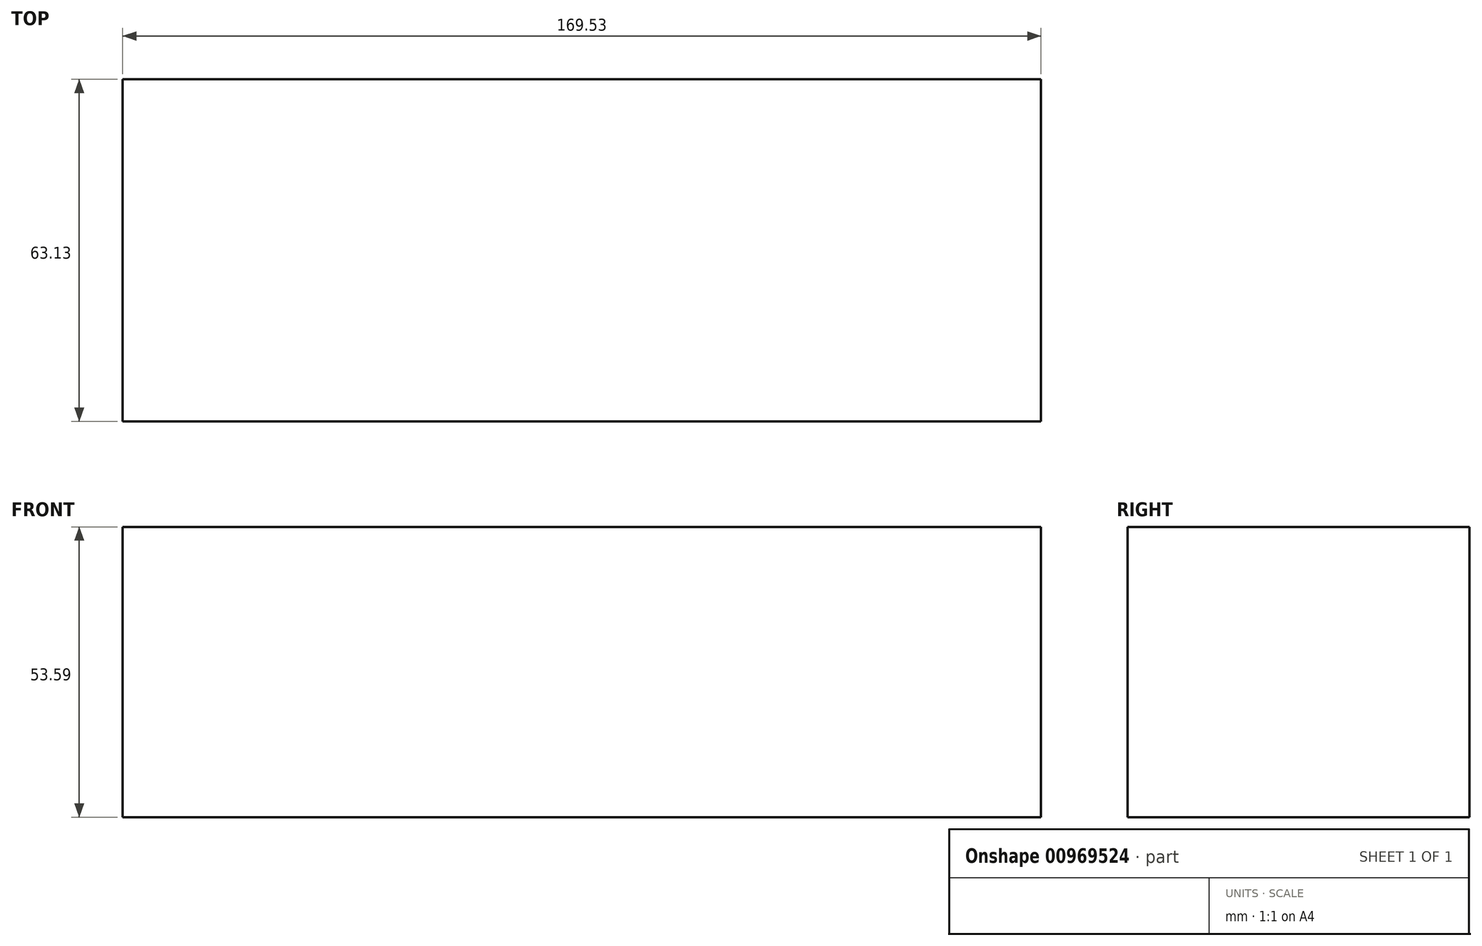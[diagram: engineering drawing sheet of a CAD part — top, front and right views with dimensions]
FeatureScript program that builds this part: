
annotation { "Feature Type Name" : "Feature", "Feature Type Description" : "" }
export const myFeature = defineFeature(function(context is Context, id is Id, definition is map)
    precondition{}
    {
        {
            var Q0;
            Q0=qCreatedBy(makeId("Top.planeOp"),FACE);
            var sketch = newSketch(context, id + "F0", { "sketchPlane" : qUnion([Q0])});
            skLineSegment(sketch, "E0.bottom", {"start": v(-103.93, -21.12) * mm, "end": v(65.6, -21.12) * mm});
            skLineSegment(sketch, "E0.top", {"start": v(-103.93, 42) * mm, "end": v(65.6, 42) * mm});
            skLineSegment(sketch, "E0.left", {"start": v(-103.93, -21.12) * mm, "end": v(-103.93, 42) * mm});
            skLineSegment(sketch, "E0.right", {"start": v(65.6, -21.12) * mm, "end": v(65.6, 42) * mm});
            skSolve(sketch);
        }
        {
            var Q0;
            Q0=makeQuery(id+"F0.imprint","IMPRINT",FACE,{"disambiguationData":[TD([[makeQuery(id+"F0.imprint","IMPRINT",EDGE,{"derivedFrom":sQuery(id+"F0.wireOp",EDGE,"E0.bottom")}),1.0]])]});
            extrude(context, id + "F1", {"entities" : qUnion([Q0]), "depth" : 53.6 * mm, "offsetDistance" : 25.4 * mm});
        }
    });
